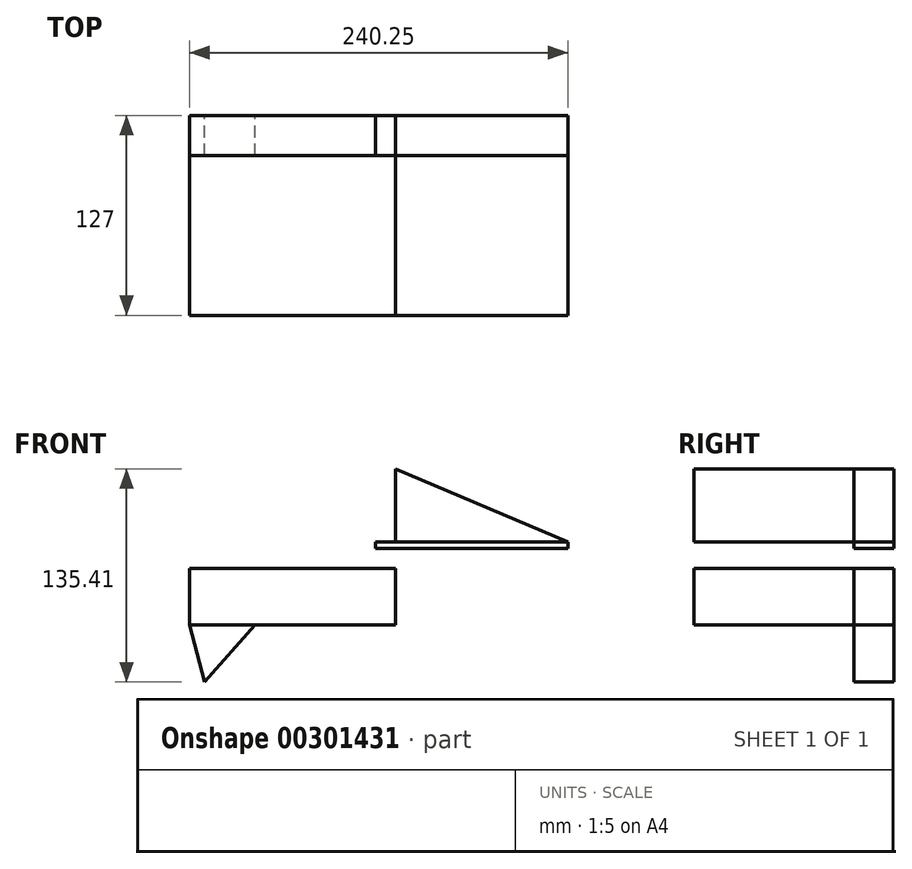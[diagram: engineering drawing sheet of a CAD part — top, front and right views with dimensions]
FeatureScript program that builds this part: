
annotation { "Feature Type Name" : "Feature", "Feature Type Description" : "" }
export const myFeature = defineFeature(function(context is Context, id is Id, definition is map)
    precondition{}
    {
        {
            var Q0;
            Q0=qCreatedBy(makeId("Front.planeOp"),FACE);
            var sketch = newSketch(context, id + "F0", { "sketchPlane" : qUnion([Q0])});
            skLineSegment(sketch, "E0.bottom", {"start": v(-65.33, -17.91) * mm, "end": v(65.33, -17.91) * mm});
            skLineSegment(sketch, "E0.top", {"start": v(-65.33, 17.91) * mm, "end": v(65.33, 17.91) * mm});
            skLineSegment(sketch, "E0.left", {"start": v(-65.33, -17.91) * mm, "end": v(-65.33, 17.91) * mm});
            skLineSegment(sketch, "E0.right", {"start": v(65.33, -17.91) * mm, "end": v(65.33, 17.91) * mm});
            skPoint(sketch, "E0.middle", {"position": v(0, 0) * mm});
            skLineSegment(sketch, "E1.bottom", {"start": v(52.69, 30.56) * mm, "end": v(174.92, 30.56) * mm});
            skLineSegment(sketch, "E1.top", {"start": v(52.69, 34.77) * mm, "end": v(174.92, 34.77) * mm});
            skLineSegment(sketch, "E1.left", {"start": v(52.69, 30.56) * mm, "end": v(52.69, 34.77) * mm});
            skLineSegment(sketch, "E1.right", {"start": v(174.92, 30.56) * mm, "end": v(174.92, 34.77) * mm});
            skPoint(sketch, "E1.middle", {"position": v(113.8, 32.67) * mm});
            skLineSegment(sketch, "E2", {"start": v(65.33, 17.91) * mm, "end": v(65.33, 76.4) * mm});
            skLineSegment(sketch, "E3", {"start": v(65.33, 81.14) * mm, "end": v(174.92, 34.77) * mm});
            skLineSegment(sketch, "E4", {"start": v(65.33, 76.4) * mm, "end": v(65.33, 81.14) * mm});
            skLineSegment(sketch, "E5", {"start": v(-23.7, -17.91) * mm, "end": v(-55.85, -54.27) * mm});
            skLineSegment(sketch, "E6", {"start": v(-55.85, -54.27) * mm, "end": v(-65.33, -17.91) * mm});
            skSolve(sketch);
        }
        {
            var Q0;
            Q0=makeQuery(id+"F0.imprint","IMPRINT",FACE,{"disambiguationData":[TD([[makeQuery(id+"F0.imprint","IMPRINT",EDGE,{"derivedFrom":sQuery(id+"F0.wireOp",EDGE,"E0.top")}),-1.0]])]});
            var Q1;
            {var subQ0=sQuery(id+"F0.wireOp",EDGE,"E3");Q1=makeQuery(id+"F0.imprint","IMPRINT",FACE,{"disambiguationData":[TD([[makeQuery(id+"F0.imprint","IMPRINT",EDGE,{"derivedFrom":subQ0}),-1.0]])]});}
            extrude(context, id + "F1", {"entities" : qUnion([Q0, Q1]), "depth" : 127 * mm});
        }
        {
            var Q0;
            Q0 = qSketchRegion(id + "F0", true);
            extrude(context, id + "F2", {"entities" : qUnion([Q0]), "depth" : 25.4 * mm});
        }
    });
